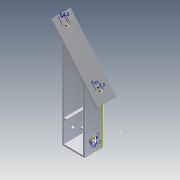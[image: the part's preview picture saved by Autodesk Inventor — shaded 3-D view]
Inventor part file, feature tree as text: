
AUTODESK INVENTOR PART (.ipt)
format: ipt  version: 2011 (Build 150239000, 239)  size: 229,376 bytes
history: native  units: mm
features: extrude x12, sketch x9, draft x3, plane x2, mirror x2
ambient origin geometry x8: Origin, YZ Plane, XZ Plane, XY Plane, X Axis, Y Axis, Z Axis, Center Point
bodies: Solid1 (feature_tree)
feature tree (28):
  extrude  "Extrusion1"  Depth=21.0mm
  plane  "Work Plane1"
  sketch  "Sketch3"  dims[d5=1.75mm d6=40.0mm d7=0.0mm]
  plane  "Work Plane2"
  extrude  "Extrusion2"  Depth=1.75mm
  extrude  "Extrusion3"  Depth=40.0mm TaperAngle=0.0deg
  extrude  "Extrusion4"  [1 undecoded]
  mirror  "Mirror1"
  extrude  "Extrusion6"  Depth=22.75mm
  sketch  "Sketch9"  dims[d14=1.75mm d15=0.0mm d16=23.3mm]
  extrude  "Extrusion7"  Depth=22.75mm
  extrude  "Extrusion8"  Depth=23.3mm
  draft  "FaceDraft1"
  extrude  "Extrusion9"  Depth=1.75mm TaperAngle=0.0deg
  extrude  "Extrusion10"  Depth=3.4mm
  draft  "FaceDraft2"
  sketch  "Sketch10"  dims[d17=3.4mm d18=1.75mm d19=0.0mm]
  extrude  "Extrusion11"  Depth=10.5mm
  extrude  "Extrusion12"  Depth=10.5mm
  draft  "FaceDraft3"
  extrude  "Extrusion13"  Depth=10.0mm TaperAngle=0.0deg
  mirror  "Mirror2"
  sketch  "Sketch1"  dims[d0=24.8mm d1=21.0mm]
  sketch  "Sketch2"  dims[d2=1.75mm d3=0.0mm d4=1.75mm]
  sketch  "Sketch4"  dims[d8=82.5mm d9=-8.726646mm]
  sketch  "Sketch5"  dims[d10=1.75mm d11=22.75mm]
  sketch  "Sketch8"  dims[d12=1.75mm d13=22.75mm]
  sketch  "Sketch11"  dims[d25=3.4mm d26=3.4mm d27=10.5mm d28=10.5mm d29=10.0mm d30=0.0mm d31=5.6mm d32=1.5mm d33=0.75mm d34=0.0mm d35=1.55mm d36=0.0mm d37=45.0deg d38=5.6mm d39=1.5mm d40=0.75mm d41=0.0mm d42=1.55mm d43=0.0mm d44=45.0deg d45=5.6mm d46=1.5mm d47=0.75mm d48=0.0mm d49=1.55mm d50=0.0mm d51=45.0deg d52=1.75mm d53=23.6mm d54=3.0mm d55=0.0mm]
note: 1 required parameter value undecoded (feature->parameter linkage not recoverable at this tier; creation-order binding heuristic only, values carry confidence <= 0.55)
